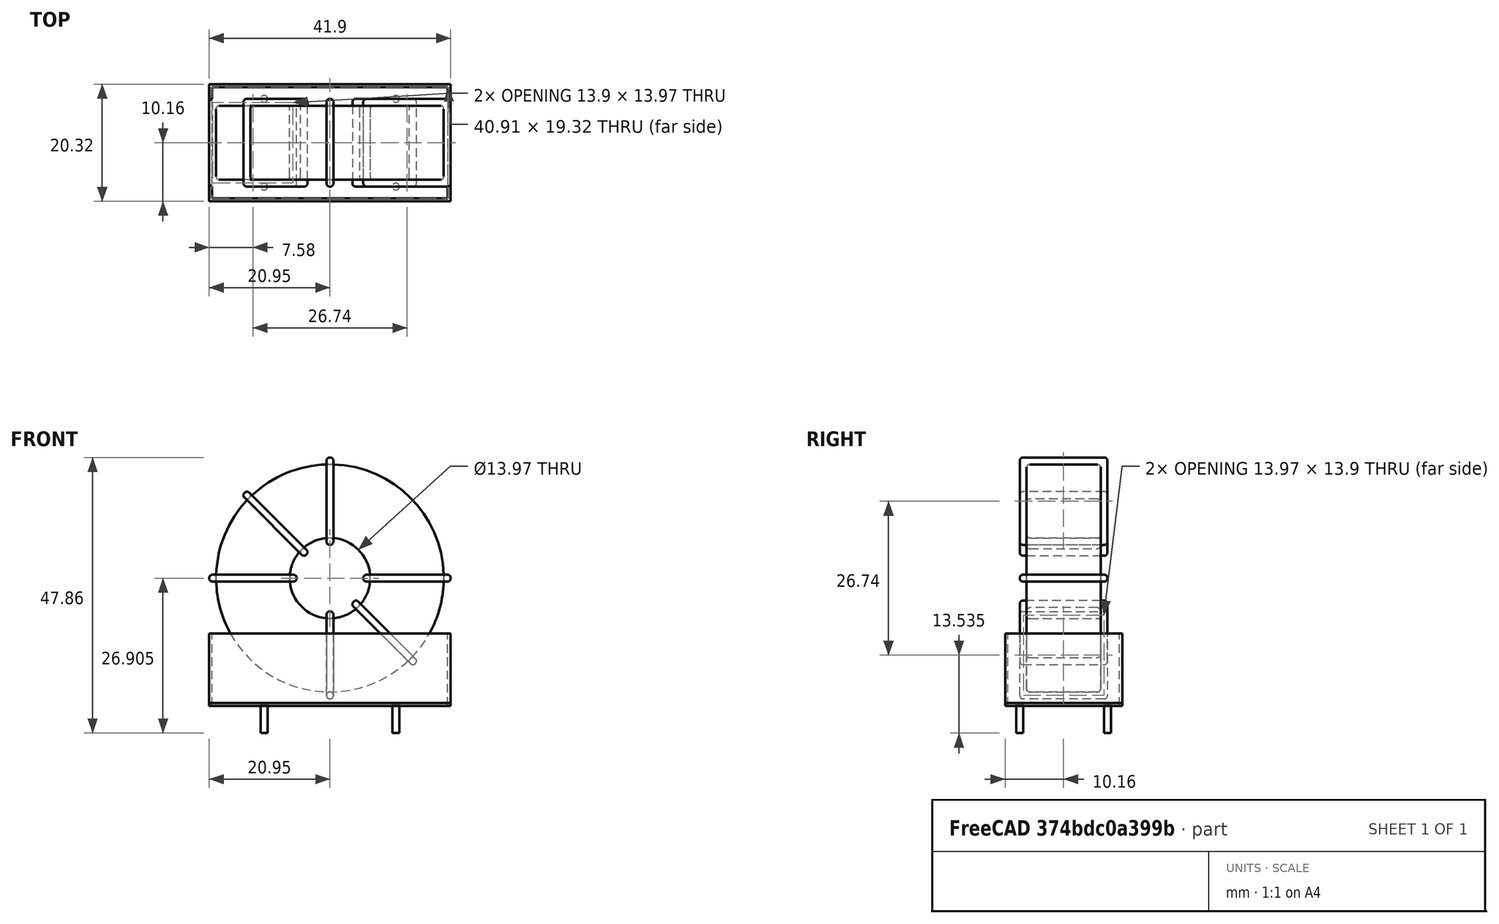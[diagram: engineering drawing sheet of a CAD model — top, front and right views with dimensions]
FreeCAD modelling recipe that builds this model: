
FCSTD DOCUMENT  (FreeCAD 0.16R6703 (Git))
Label: L_CommonModeChoke_Toroid_Vertical_L41.9mm_W20.3mm_Px15.24mm_Py22.86mm_Bourns_8100series
License: All rights reserved
LicenseURL: http://en.wikipedia.org/wiki/All_rights_reserved
objects: Sketcher::SketchObject×8, PartDesign::Pad×8, PartDesign::Fillet×5, Spreadsheet::Sheet×1
note: 29 computed .brp shape members not serialized (recipe doc carries the construction recipe); baked Part::Feature solids carry a one-line shape summary decoded from their .brp

FEATURE [Spreadsheet::Sheet] Spreadsheet  label="dimensions"
  cells = A1=Wx; B1(Wx)=41.91; C1(WW)=13.97; D1(iWx)=41.91; A2=Wy; B2(Wy)=15.24; D2(iWy)=20.32; A3=RM; B3(RMx)=15.24; C3(RMy)=22.86; A4=d_wire; B4(d_wire)=1.2; A5=H; B5(H)=31; A6=offsetx; B6(offsetx)=9.524999999999999
FEATURE [Sketcher::SketchObject] Sketch
  Placement = pos=(11.43,-7.62,0) rot=(1,0,0;1.5708rad)
  expr: Placement.Base.x = Spreadsheet.RMy / 2
  expr: Constraints[4] = Spreadsheet.WW / 2
  expr: Placement.Base.y = -Spreadsheet.RMx / 2
  expr: Constraints[0] = Spreadsheet.Wx / 2 - Spreadsheet.d_wire
  expr: Constraints[2] = Spreadsheet.Wx / 2 + Spreadsheet.d_wire + 0.5
  sketch-geometry (2):
    g0: Circle CenterX=0 CenterY=22.655 CenterZ=0 NormalX=0 NormalY=0 NormalZ=1 Radius=19.755
    g1: Circle CenterX=0 CenterY=22.655 CenterZ=0 NormalX=0 NormalY=0 NormalZ=1 Radius=6.985
  constraints (5):
    c: Radius(g0) = 19.755
    c: DistanceX(g-1,g0) = 0
    c: DistanceY(g-1,g0) = 22.655
    c: Coincident(g1,g0)
    c: Radius(g1) = 6.985
FEATURE [PartDesign::Pad] Pad
  Length = 12.84
  Length2 = 100
  Midplane = true
  Placement = pos=(11.43,-7.62,0) rot=(1,0,0;1.5708rad)
  Sketch = -> Sketch
  Type = 0
  expr: Length = Spreadsheet.Wy - 2 * Spreadsheet.d_wire
FEATURE [Sketcher::SketchObject] Sketch001
  Placement = pos=(0,0,0.75) rot=(0,0,1;0rad)
  expr: Constraints[4] = Spreadsheet.RMy
  expr: Constraints[2] = -Spreadsheet.RMx
  expr: Constraints[1] = Spreadsheet.d_wire / 2
  sketch-geometry (4):
    g0: Circle CenterX=0 CenterY=0 CenterZ=0 NormalX=0 NormalY=0 NormalZ=1 Radius=0.6
    g1: Circle CenterX=22.86 CenterY=-15.24 CenterZ=0 NormalX=0 NormalY=0 NormalZ=1 Radius=0.6
    g2: Circle CenterX=0 CenterY=-15.24 CenterZ=0 NormalX=0 NormalY=0 NormalZ=1 Radius=0.6
    g3: Circle CenterX=22.86 CenterY=0 CenterZ=0 NormalX=0 NormalY=0 NormalZ=1 Radius=0.6
  constraints (11):
    c: Equal(g0,g1)
    c: Radius(g0) = 0.6
    c: DistanceY(g-1,g1) = -15.24
    c: Coincident(g0,g-1)
    c: DistanceX(g-1,g1) = 22.86
    c: PointOnObject(g2,g-2)
    c: DistanceY(g-1,g3) = 0
    c: DistanceY(g2,g1) = 0
    c: DistanceX(g3,g1) = 0
    c: Equal(g3,g2)
    c: Equal(g2,g1)
FEATURE [PartDesign::Pad] Pad001
  Length = 5
  Length2 = 0
  Placement = pos=(0,0,0.75) rot=(0,0,1;0rad)
  Reversed = true
  Sketch = -> Sketch001
  Type = 0
FEATURE [PartDesign::Fillet] Fillet
  Base = -> Pad [Edge6,Edge3,Edge2]
  Placement = pos=(11.43,-7.62,0) rot=(1,0,0;1.5708rad)
  Radius = 0.5
FEATURE [Sketcher::SketchObject] Sketch003
  Placement = pos=(11.43,0,22.655) rot=(1,0,0;3.14159rad)
  expr: Placement.Base.x = Spreadsheet.RMy / 2
  expr: Constraints[18] = Spreadsheet.d_wire
  expr: Constraints[16] = Spreadsheet.d_wire
  expr: Constraints[19] = Spreadsheet.d_wire
  expr: Constraints[17] = Spreadsheet.d_wire
  expr: Placement.Base.y = -1 * (Spreadsheet.RMx - Spreadsheet.Wy) / 2
  expr: Constraints[21] = (Spreadsheet.Wx - Spreadsheet.WW) / 2 - Spreadsheet.d_wire
  expr: Constraints[22] = Spreadsheet.Wx / 2 - Spreadsheet.d_wire
  expr: Constraints[43] = Spreadsheet.d_wire
  expr: Constraints[48] = Spreadsheet.Wx - Spreadsheet.d_wire * 2
  expr: Constraints[49] = Spreadsheet.Wy
  expr: Placement.Base.z = Spreadsheet.Wx / 2 + Spreadsheet.d_wire + 0.5
  sketch-geometry (16):
    g0: LineSegment StartX=-5.785 StartY=0 StartZ=0 EndX=-20.955 EndY=0 EndZ=0
    g1: LineSegment StartX=-20.955 StartY=0 StartZ=0 EndX=-20.955 EndY=15.24 EndZ=0
    g2: LineSegment StartX=-20.955 StartY=15.24 StartZ=0 EndX=-5.785 EndY=15.24 EndZ=0
    g3: LineSegment StartX=-5.785 StartY=15.24 StartZ=0 EndX=-5.785 EndY=0 EndZ=0
    g4: LineSegment StartX=-19.755 StartY=14.04 StartZ=0 EndX=-6.985 EndY=14.04 EndZ=0
    g5: LineSegment StartX=-6.985 StartY=14.04 StartZ=0 EndX=-6.985 EndY=1.2 EndZ=0
    g6: LineSegment StartX=-6.985 StartY=1.2 StartZ=0 EndX=-19.755 EndY=1.2 EndZ=0
    g7: LineSegment StartX=-19.755 StartY=1.2 StartZ=0 EndX=-19.755 EndY=14.04 EndZ=0
    g8: LineSegment StartX=5.785 StartY=15.24 StartZ=0 EndX=20.955 EndY=15.24 EndZ=0
    g9: LineSegment StartX=20.955 StartY=15.24 StartZ=0 EndX=20.955 EndY=0 EndZ=0
    g10: LineSegment StartX=20.955 StartY=0 StartZ=0 EndX=5.785 EndY=0 EndZ=0
    g11: LineSegment StartX=5.785 StartY=0 StartZ=0 EndX=5.785 EndY=15.24 EndZ=0
    g12: LineSegment StartX=6.985 StartY=14.04 StartZ=0 EndX=19.755 EndY=14.04 EndZ=0
    g13: LineSegment StartX=19.755 StartY=14.04 StartZ=0 EndX=19.755 EndY=1.2 EndZ=0
    g14: LineSegment StartX=19.755 StartY=1.2 StartZ=0 EndX=6.985 EndY=1.2 EndZ=0
    g15: LineSegment StartX=6.985 StartY=1.2 StartZ=0 EndX=6.985 EndY=14.04 EndZ=0
  constraints (50):
    c: Horizontal(g0)
    c: Coincident(g1,g0)
    c: Vertical(g1)
    c: Coincident(g2,g1)
    c: Horizontal(g2)
    c: Coincident(g3,g2)
    c: Coincident(g3,g0)
    c: Vertical(g3)
    c: Coincident(g4,g5)
    c: Coincident(g5,g6)
    c: Coincident(g6,g7)
    c: Coincident(g7,g4)
    c: Horizontal(g4)
    c: Horizontal(g6)
    c: Vertical(g5)
    c: Vertical(g7)
    c: DistanceX(g1,g4) = 1.2
    c: DistanceY(g4,g1) = 1.2
    c: DistanceX(g5,g0) = 1.2
    c: DistanceY(g0,g5) = 1.2
    c: DistanceY(g-1,g0) = 0
    c: DistanceX(g6,g6) = 12.77
    c: DistanceX(g6,g-1) = 19.755
    c: Coincident(g8,g9)
    c: Coincident(g9,g10)
    c: Coincident(g10,g11)
    c: Coincident(g11,g8)
    c: Horizontal(g8)
    c: Horizontal(g10)
    c: Vertical(g9)
    c: Vertical(g11)
    c: Coincident(g12,g13)
    c: Coincident(g13,g14)
    c: Coincident(g14,g15)
    c: Coincident(g15,g12)
    c: Horizontal(g12)
    c: Horizontal(g14)
    c: Vertical(g13)
    c: Vertical(g15)
    c: DistanceY(g8,g2) = 0
    c: DistanceY(g10,g0) = 0
    c: DistanceY(g14,g5) = 0
    c: DistanceY(g12,g4) = 0
    c: DistanceX(g8,g12) = 1.2
    c: Equal(g8,g2)
    c: Equal(g12,g4)
    c: Equal(g9,g1)
    c: Equal(g13,g7)
    c: DistanceX(g4,g12) = 39.51
    c: DistanceY(g0,g1) = 15.24
FEATURE [PartDesign::Pad] Pad002
  Length = 1.2
  Length2 = 100
  Midplane = true
  Placement = pos=(11.43,0,22.655) rot=(1,0,0;3.14159rad)
  Sketch = -> Sketch003
  Type = 0
  expr: Length = Spreadsheet.d_wire
FEATURE [PartDesign::Fillet] Fillet001
  Base = -> Pad002 [Edge38,Edge41,Edge42,Edge43,Edge29,Edge32,Edge33,Edge34,Edge25,Edge35,Edge36,Edge13,Edge14,Edge15,Edge16,Edge17,Edge18,Edge19,Edge1,Edge2,Edge3,Edge4,Edge5,Edge6,Edge7,Edge37,Edge39,Edge40,Edge20,Edge23,Edge24,Edge21,Edge22,Edge8,Edge9,Edge10,Edge11,Edge12,Edge26,Edge27,+8 more]
  Placement = pos=(11.43,0,22.655) rot=(1,0,0;3.14159rad)
  Radius = 0.564
  expr: Radius = Spreadsheet.d_wire * 0.47
FEATURE [Sketcher::SketchObject] Sketch004
  Placement = pos=(11.43,0,22.655) rot=(0.92388,0,0.382683;3.14159rad)
  expr: Placement.Base.x = Spreadsheet.RMy / 2
  expr: Constraints[18] = Spreadsheet.d_wire
  expr: Constraints[16] = Spreadsheet.d_wire
  expr: Constraints[19] = Spreadsheet.d_wire
  expr: Constraints[17] = Spreadsheet.d_wire
  expr: Placement.Base.y = -1 * (Spreadsheet.RMx - Spreadsheet.Wy) / 2
  expr: Constraints[21] = (Spreadsheet.Wx - Spreadsheet.WW) / 2 - Spreadsheet.d_wire
  expr: Constraints[22] = Spreadsheet.Wx / 2 - Spreadsheet.d_wire
  expr: Constraints[43] = Spreadsheet.d_wire
  expr: Constraints[48] = Spreadsheet.Wx - 2 * Spreadsheet.d_wire
  expr: Constraints[49] = Spreadsheet.Wy
  expr: Placement.Base.z = Spreadsheet.Wx / 2 + Spreadsheet.d_wire + 0.5
  sketch-geometry (16):
    g0: LineSegment StartX=-5.785 StartY=0 StartZ=0 EndX=-20.955 EndY=0 EndZ=0
    g1: LineSegment StartX=-20.955 StartY=0 StartZ=0 EndX=-20.955 EndY=15.24 EndZ=0
    g2: LineSegment StartX=-20.955 StartY=15.24 StartZ=0 EndX=-5.785 EndY=15.24 EndZ=0
    g3: LineSegment StartX=-5.785 StartY=15.24 StartZ=0 EndX=-5.785 EndY=0 EndZ=0
    g4: LineSegment StartX=-19.755 StartY=14.04 StartZ=0 EndX=-6.985 EndY=14.04 EndZ=0
    g5: LineSegment StartX=-6.985 StartY=14.04 StartZ=0 EndX=-6.985 EndY=1.2 EndZ=0
    g6: LineSegment StartX=-6.985 StartY=1.2 StartZ=0 EndX=-19.755 EndY=1.2 EndZ=0
    g7: LineSegment StartX=-19.755 StartY=1.2 StartZ=0 EndX=-19.755 EndY=14.04 EndZ=0
    g8: LineSegment StartX=5.785 StartY=15.24 StartZ=0 EndX=20.955 EndY=15.24 EndZ=0
    g9: LineSegment StartX=20.955 StartY=15.24 StartZ=0 EndX=20.955 EndY=0 EndZ=0
    g10: LineSegment StartX=20.955 StartY=0 StartZ=0 EndX=5.785 EndY=0 EndZ=0
    g11: LineSegment StartX=5.785 StartY=0 StartZ=0 EndX=5.785 EndY=15.24 EndZ=0
    g12: LineSegment StartX=6.985 StartY=14.04 StartZ=0 EndX=19.755 EndY=14.04 EndZ=0
    g13: LineSegment StartX=19.755 StartY=14.04 StartZ=0 EndX=19.755 EndY=1.2 EndZ=0
    g14: LineSegment StartX=19.755 StartY=1.2 StartZ=0 EndX=6.985 EndY=1.2 EndZ=0
    g15: LineSegment StartX=6.985 StartY=1.2 StartZ=0 EndX=6.985 EndY=14.04 EndZ=0
  constraints (50):
    c: Horizontal(g0)
    c: Coincident(g1,g0)
    c: Vertical(g1)
    c: Coincident(g2,g1)
    c: Horizontal(g2)
    c: Coincident(g3,g2)
    c: Coincident(g3,g0)
    c: Vertical(g3)
    c: Coincident(g4,g5)
    c: Coincident(g5,g6)
    c: Coincident(g6,g7)
    c: Coincident(g7,g4)
    c: Horizontal(g4)
    c: Horizontal(g6)
    c: Vertical(g5)
    c: Vertical(g7)
    c: DistanceX(g1,g4) = 1.2
    c: DistanceY(g4,g1) = 1.2
    c: DistanceX(g5,g0) = 1.2
    c: DistanceY(g0,g5) = 1.2
    c: DistanceY(g-1,g0) = 0
    c: DistanceX(g6,g6) = 12.77
    c: DistanceX(g6,g-1) = 19.755
    c: Coincident(g8,g9)
    c: Coincident(g9,g10)
    c: Coincident(g10,g11)
    c: Coincident(g11,g8)
    c: Horizontal(g8)
    c: Horizontal(g10)
    c: Vertical(g9)
    c: Vertical(g11)
    c: Coincident(g12,g13)
    c: Coincident(g13,g14)
    c: Coincident(g14,g15)
    c: Coincident(g15,g12)
    c: Horizontal(g12)
    c: Horizontal(g14)
    c: Vertical(g13)
    c: Vertical(g15)
    c: DistanceY(g8,g2) = 0
    c: DistanceY(g10,g0) = 0
    c: DistanceY(g14,g5) = 0
    c: DistanceY(g12,g4) = 0
    c: DistanceX(g8,g12) = 1.2
    c: Equal(g8,g2)
    c: Equal(g12,g4)
    c: Equal(g9,g1)
    c: Equal(g13,g7)
    c: DistanceX(g4,g12) = 39.51
    c: DistanceY(g0,g1) = 15.24
FEATURE [PartDesign::Pad] Pad003
  Length = 1.2
  Length2 = 100
  Midplane = true
  Placement = pos=(11.43,0,22.655) rot=(0.92388,0,0.382683;3.14159rad)
  Sketch = -> Sketch004
  Type = 0
  expr: Length = Spreadsheet.d_wire
FEATURE [PartDesign::Fillet] Fillet002
  Base = -> Pad003 [Edge38,Edge41,Edge42,Edge43,Edge29,Edge32,Edge33,Edge34,Edge25,Edge35,Edge36,Edge13,Edge14,Edge15,Edge16,Edge17,Edge18,Edge19,Edge1,Edge2,Edge3,Edge4,Edge5,Edge6,Edge7,Edge37,Edge39,Edge40,Edge20,Edge23,Edge24,Edge21,Edge22,Edge8,Edge9,Edge10,Edge11,Edge12,Edge26,Edge27,+8 more]
  Placement = pos=(11.43,0,22.655) rot=(0.92388,0,0.382683;3.14159rad)
  Radius = 0.564
  expr: Radius = Spreadsheet.d_wire * 0.47
FEATURE [Sketcher::SketchObject] Sketch005
  Placement = pos=(11.43,0,22.655) rot=(0.92388,0,-0.382683;3.14159rad)
  expr: Placement.Base.x = Spreadsheet.RMy / 2
  expr: Constraints[18] = Spreadsheet.d_wire
  expr: Constraints[16] = Spreadsheet.d_wire
  expr: Constraints[19] = Spreadsheet.d_wire
  expr: Constraints[17] = Spreadsheet.d_wire
  expr: Placement.Base.y = -1 * (Spreadsheet.RMx - Spreadsheet.Wy) / 2
  expr: Constraints[21] = (Spreadsheet.Wx - Spreadsheet.WW) / 2 - Spreadsheet.d_wire
  expr: Constraints[22] = Spreadsheet.Wx / 2 - Spreadsheet.d_wire
  expr: Constraints[43] = Spreadsheet.d_wire
  expr: Constraints[48] = Spreadsheet.Wx - 2 * Spreadsheet.d_wire
  expr: Constraints[49] = Spreadsheet.Wy
  expr: Placement.Base.z = Spreadsheet.Wx / 2 + Spreadsheet.d_wire + 0.5
  sketch-geometry (16):
    g0: LineSegment StartX=-5.785 StartY=0 StartZ=0 EndX=-20.955 EndY=0 EndZ=0
    g1: LineSegment StartX=-20.955 StartY=0 StartZ=0 EndX=-20.955 EndY=15.24 EndZ=0
    g2: LineSegment StartX=-20.955 StartY=15.24 StartZ=0 EndX=-5.785 EndY=15.24 EndZ=0
    g3: LineSegment StartX=-5.785 StartY=15.24 StartZ=0 EndX=-5.785 EndY=0 EndZ=0
    g4: LineSegment StartX=-19.755 StartY=14.04 StartZ=0 EndX=-6.985 EndY=14.04 EndZ=0
    g5: LineSegment StartX=-6.985 StartY=14.04 StartZ=0 EndX=-6.985 EndY=1.2 EndZ=0
    g6: LineSegment StartX=-6.985 StartY=1.2 StartZ=0 EndX=-19.755 EndY=1.2 EndZ=0
    g7: LineSegment StartX=-19.755 StartY=1.2 StartZ=0 EndX=-19.755 EndY=14.04 EndZ=0
    g8: LineSegment StartX=5.785 StartY=15.24 StartZ=0 EndX=20.955 EndY=15.24 EndZ=0
    g9: LineSegment StartX=20.955 StartY=15.24 StartZ=0 EndX=20.955 EndY=0 EndZ=0
    g10: LineSegment StartX=20.955 StartY=0 StartZ=0 EndX=5.785 EndY=0 EndZ=0
    g11: LineSegment StartX=5.785 StartY=0 StartZ=0 EndX=5.785 EndY=15.24 EndZ=0
    g12: LineSegment StartX=6.985 StartY=14.04 StartZ=0 EndX=19.755 EndY=14.04 EndZ=0
    g13: LineSegment StartX=19.755 StartY=14.04 StartZ=0 EndX=19.755 EndY=1.2 EndZ=0
    g14: LineSegment StartX=19.755 StartY=1.2 StartZ=0 EndX=6.985 EndY=1.2 EndZ=0
    g15: LineSegment StartX=6.985 StartY=1.2 StartZ=0 EndX=6.985 EndY=14.04 EndZ=0
  constraints (50):
    c: Horizontal(g0)
    c: Coincident(g1,g0)
    c: Vertical(g1)
    c: Coincident(g2,g1)
    c: Horizontal(g2)
    c: Coincident(g3,g2)
    c: Coincident(g3,g0)
    c: Vertical(g3)
    c: Coincident(g4,g5)
    c: Coincident(g5,g6)
    c: Coincident(g6,g7)
    c: Coincident(g7,g4)
    c: Horizontal(g4)
    c: Horizontal(g6)
    c: Vertical(g5)
    c: Vertical(g7)
    c: DistanceX(g1,g4) = 1.2
    c: DistanceY(g4,g1) = 1.2
    c: DistanceX(g5,g0) = 1.2
    c: DistanceY(g0,g5) = 1.2
    c: DistanceY(g-1,g0) = 0
    c: DistanceX(g6,g6) = 12.77
    c: DistanceX(g6,g-1) = 19.755
    c: Coincident(g8,g9)
    c: Coincident(g9,g10)
    c: Coincident(g10,g11)
    c: Coincident(g11,g8)
    c: Horizontal(g8)
    c: Horizontal(g10)
    c: Vertical(g9)
    c: Vertical(g11)
    c: Coincident(g12,g13)
    c: Coincident(g13,g14)
    c: Coincident(g14,g15)
    c: Coincident(g15,g12)
    c: Horizontal(g12)
    c: Horizontal(g14)
    c: Vertical(g13)
    c: Vertical(g15)
    c: DistanceY(g8,g2) = 0
    c: DistanceY(g10,g0) = 0
    c: DistanceY(g14,g5) = 0
    c: DistanceY(g12,g4) = 0
    c: DistanceX(g8,g12) = 1.2
    c: Equal(g8,g2)
    c: Equal(g12,g4)
    c: Equal(g9,g1)
    c: Equal(g13,g7)
    c: DistanceX(g4,g12) = 39.51
    c: DistanceY(g0,g1) = 15.24
FEATURE [PartDesign::Pad] Pad004
  Length = 1.2
  Length2 = 100
  Midplane = true
  Placement = pos=(11.43,0,22.655) rot=(0.92388,0,-0.382683;3.14159rad)
  Sketch = -> Sketch005
  Type = 0
  expr: Length = Spreadsheet.d_wire
FEATURE [PartDesign::Fillet] Fillet003
  Base = -> Pad004 [Edge38,Edge41,Edge42,Edge43,Edge29,Edge32,Edge33,Edge34,Edge25,Edge35,Edge36,Edge13,Edge14,Edge15,Edge16,Edge17,Edge18,Edge19,Edge1,Edge2,Edge3,Edge4,Edge5,Edge6,Edge7,Edge37,Edge39,Edge40,Edge20,Edge23,Edge24,Edge21,Edge22,Edge8,Edge9,Edge10,Edge11,Edge12,Edge26,Edge27,+8 more]
  Placement = pos=(11.43,0,22.655) rot=(0.92388,0,-0.382683;3.14159rad)
  Radius = 0.564
  expr: Radius = Spreadsheet.d_wire * 0.47
FEATURE [Sketcher::SketchObject] Sketch006
  Placement = pos=(11.43,0,22.655) rot=(0.707107,0,0.707107;3.14159rad)
  expr: Placement.Base.x = Spreadsheet.RMy / 2
  expr: Constraints[18] = Spreadsheet.d_wire
  expr: Constraints[16] = Spreadsheet.d_wire
  expr: Constraints[19] = Spreadsheet.d_wire
  expr: Constraints[17] = Spreadsheet.d_wire
  expr: Placement.Base.y = -1 * (Spreadsheet.RMx - Spreadsheet.Wy) / 2
  expr: Constraints[21] = (Spreadsheet.Wx - Spreadsheet.WW) / 2 - Spreadsheet.d_wire
  expr: Constraints[22] = Spreadsheet.Wx / 2 - Spreadsheet.d_wire
  expr: Constraints[43] = Spreadsheet.d_wire
  expr: Constraints[48] = Spreadsheet.Wx - Spreadsheet.d_wire * 2
  expr: Constraints[49] = Spreadsheet.Wy
  expr: Placement.Base.z = Spreadsheet.Wx / 2 + Spreadsheet.d_wire + 0.5
  sketch-geometry (16):
    g0: LineSegment StartX=-5.785 StartY=0 StartZ=0 EndX=-20.955 EndY=0 EndZ=0
    g1: LineSegment StartX=-20.955 StartY=0 StartZ=0 EndX=-20.955 EndY=15.24 EndZ=0
    g2: LineSegment StartX=-20.955 StartY=15.24 StartZ=0 EndX=-5.785 EndY=15.24 EndZ=0
    g3: LineSegment StartX=-5.785 StartY=15.24 StartZ=0 EndX=-5.785 EndY=0 EndZ=0
    g4: LineSegment StartX=-19.755 StartY=14.04 StartZ=0 EndX=-6.985 EndY=14.04 EndZ=0
    g5: LineSegment StartX=-6.985 StartY=14.04 StartZ=0 EndX=-6.985 EndY=1.2 EndZ=0
    g6: LineSegment StartX=-6.985 StartY=1.2 StartZ=0 EndX=-19.755 EndY=1.2 EndZ=0
    g7: LineSegment StartX=-19.755 StartY=1.2 StartZ=0 EndX=-19.755 EndY=14.04 EndZ=0
    g8: LineSegment StartX=5.785 StartY=15.24 StartZ=0 EndX=20.955 EndY=15.24 EndZ=0
    g9: LineSegment StartX=20.955 StartY=15.24 StartZ=0 EndX=20.955 EndY=0 EndZ=0
    g10: LineSegment StartX=20.955 StartY=0 StartZ=0 EndX=5.785 EndY=0 EndZ=0
    g11: LineSegment StartX=5.785 StartY=0 StartZ=0 EndX=5.785 EndY=15.24 EndZ=0
    g12: LineSegment StartX=6.985 StartY=14.04 StartZ=0 EndX=19.755 EndY=14.04 EndZ=0
    g13: LineSegment StartX=19.755 StartY=14.04 StartZ=0 EndX=19.755 EndY=1.2 EndZ=0
    g14: LineSegment StartX=19.755 StartY=1.2 StartZ=0 EndX=6.985 EndY=1.2 EndZ=0
    g15: LineSegment StartX=6.985 StartY=1.2 StartZ=0 EndX=6.985 EndY=14.04 EndZ=0
  constraints (50):
    c: Horizontal(g0)
    c: Coincident(g1,g0)
    c: Vertical(g1)
    c: Coincident(g2,g1)
    c: Horizontal(g2)
    c: Coincident(g3,g2)
    c: Coincident(g3,g0)
    c: Vertical(g3)
    c: Coincident(g4,g5)
    c: Coincident(g5,g6)
    c: Coincident(g6,g7)
    c: Coincident(g7,g4)
    c: Horizontal(g4)
    c: Horizontal(g6)
    c: Vertical(g5)
    c: Vertical(g7)
    c: DistanceX(g1,g4) = 1.2
    c: DistanceY(g4,g1) = 1.2
    c: DistanceX(g5,g0) = 1.2
    c: DistanceY(g0,g5) = 1.2
    c: DistanceY(g-1,g0) = 0
    c: DistanceX(g6,g6) = 12.77
    c: DistanceX(g6,g-1) = 19.755
    c: Coincident(g8,g9)
    c: Coincident(g9,g10)
    c: Coincident(g10,g11)
    c: Coincident(g11,g8)
    c: Horizontal(g8)
    c: Horizontal(g10)
    c: Vertical(g9)
    c: Vertical(g11)
    c: Coincident(g12,g13)
    c: Coincident(g13,g14)
    c: Coincident(g14,g15)
    c: Coincident(g15,g12)
    c: Horizontal(g12)
    c: Horizontal(g14)
    c: Vertical(g13)
    c: Vertical(g15)
    c: DistanceY(g8,g2) = 0
    c: DistanceY(g10,g0) = 0
    c: DistanceY(g14,g5) = 0
    c: DistanceY(g12,g4) = 0
    c: DistanceX(g8,g12) = 1.2
    c: Equal(g8,g2)
    c: Equal(g12,g4)
    c: Equal(g9,g1)
    c: Equal(g13,g7)
    c: DistanceX(g4,g12) = 39.51
    c: DistanceY(g0,g1) = 15.24
FEATURE [PartDesign::Pad] Pad005
  Length = 1.2
  Length2 = 100
  Midplane = true
  Placement = pos=(11.43,0,22.655) rot=(0.707107,0,0.707107;3.14159rad)
  Sketch = -> Sketch006
  Type = 0
  expr: Length = Spreadsheet.d_wire
FEATURE [PartDesign::Fillet] Fillet004
  Base = -> Pad005 [Edge38,Edge41,Edge42,Edge43,Edge29,Edge32,Edge33,Edge34,Edge25,Edge35,Edge36,Edge13,Edge14,Edge15,Edge16,Edge17,Edge18,Edge19,Edge1,Edge2,Edge3,Edge4,Edge5,Edge6,Edge7,Edge37,Edge39,Edge40,Edge20,Edge23,Edge24,Edge21,Edge22,Edge8,Edge9,Edge10,Edge11,Edge12,Edge26,Edge27,+8 more]
  Placement = pos=(11.43,0,22.655) rot=(0.707107,0,0.707107;3.14159rad)
  Radius = 0.564
  expr: Radius = Spreadsheet.d_wire * 0.47
FEATURE [Sketcher::SketchObject] Sketch007
  Placement = pos=(11.43,0,0.5) rot=(0,0,1;0rad)
  expr: Placement.Base.x = Spreadsheet.RMy / 2
  expr: Placement.Base.z = 0.5
  expr: Constraints[11] = Spreadsheet.iWx / 2
  expr: Constraints[10] = (Spreadsheet.iWy - Spreadsheet.RMx) / 2
  expr: Constraints[9] = Spreadsheet.iWy
  expr: Constraints[8] = Spreadsheet.iWx
  sketch-geometry (4):
    g0: LineSegment StartX=-20.955 StartY=2.54 StartZ=0 EndX=20.955 EndY=2.54 EndZ=0
    g1: LineSegment StartX=20.955 StartY=2.54 StartZ=0 EndX=20.955 EndY=-17.78 EndZ=0
    g2: LineSegment StartX=20.955 StartY=-17.78 StartZ=0 EndX=-20.955 EndY=-17.78 EndZ=0
    g3: LineSegment StartX=-20.955 StartY=-17.78 StartZ=0 EndX=-20.955 EndY=2.54 EndZ=0
  constraints (12):
    c: Coincident(g0,g1)
    c: Coincident(g1,g2)
    c: Coincident(g2,g3)
    c: Coincident(g3,g0)
    c: Horizontal(g0)
    c: Horizontal(g2)
    c: Vertical(g1)
    c: Vertical(g3)
    c: DistanceX(g0,g0) = 41.91
    c: DistanceY(g3,g3) = 20.32
    c: DistanceY(g-1,g0) = 2.54
    c: DistanceX(g0,g-1) = 20.955
FEATURE [PartDesign::Pad] Pad006
  Length = 0.5
  Length2 = 100
  Placement = pos=(11.43,0,0.5) rot=(0,0,1;0rad)
  Sketch = -> Sketch007
  Type = 0
FEATURE [Sketcher::SketchObject] Sketch008
  Placement = pos=(11.43,0,0.5) rot=(0,0,1;0rad)
  expr: Placement.Base.x = Spreadsheet.RMy / 2
  expr: Constraints[8] = Spreadsheet.iWx
  expr: Constraints[9] = Spreadsheet.iWy
  expr: Constraints[10] = (Spreadsheet.iWy - Spreadsheet.RMx) / 2
  expr: Placement.Base.z = 0.5
  expr: Constraints[21] = 0.5
  expr: Constraints[11] = Spreadsheet.iWx / 2
  sketch-geometry (8):
    g0: LineSegment StartX=-20.955 StartY=2.54 StartZ=0 EndX=20.955 EndY=2.54 EndZ=0
    g1: LineSegment StartX=20.955 StartY=2.54 StartZ=0 EndX=20.955 EndY=-17.78 EndZ=0
    g2: LineSegment StartX=20.955 StartY=-17.78 StartZ=0 EndX=-20.955 EndY=-17.78 EndZ=0
    g3: LineSegment StartX=-20.955 StartY=-17.78 StartZ=0 EndX=-20.955 EndY=2.54 EndZ=0
    g4: LineSegment StartX=-20.455 StartY=2.04 StartZ=0 EndX=20.455 EndY=2.04 EndZ=0
    g5: LineSegment StartX=20.455 StartY=2.04 StartZ=0 EndX=20.455 EndY=-17.28 EndZ=0
    g6: LineSegment StartX=20.455 StartY=-17.28 StartZ=0 EndX=-20.455 EndY=-17.28 EndZ=0
    g7: LineSegment StartX=-20.455 StartY=-17.28 StartZ=0 EndX=-20.455 EndY=2.04 EndZ=0
  constraints (24):
    c: Coincident(g0,g1)
    c: Coincident(g1,g2)
    c: Coincident(g2,g3)
    c: Coincident(g3,g0)
    c: Horizontal(g0)
    c: Horizontal(g2)
    c: Vertical(g1)
    c: Vertical(g3)
    c: DistanceX(g0,g0) = 41.91
    c: DistanceY(g3,g3) = 20.32
    c: DistanceY(g-1,g0) = 2.54
    c: DistanceX(g0,g-1) = 20.955
    c: Coincident(g4,g5)
    c: Coincident(g5,g6)
    c: Coincident(g6,g7)
    c: Coincident(g7,g4)
    c: Horizontal(g4)
    c: Horizontal(g6)
    c: Vertical(g5)
    c: Vertical(g7)
    c: DistanceX(g5,g1) = 0.5
    c: DistanceY(g1,g5) = 0.5
    c: DistanceX(g0,g4) = 0.5
    c: DistanceY(g4,g0) = 0.5
FEATURE [PartDesign::Pad] Pad007
  Length = 12.573
  Length2 = 100
  Placement = pos=(11.43,0,0.5) rot=(0,0,1;0rad)
  Sketch = -> Sketch008
  Type = 0
  expr: Length = Spreadsheet.Wx * 0.3
